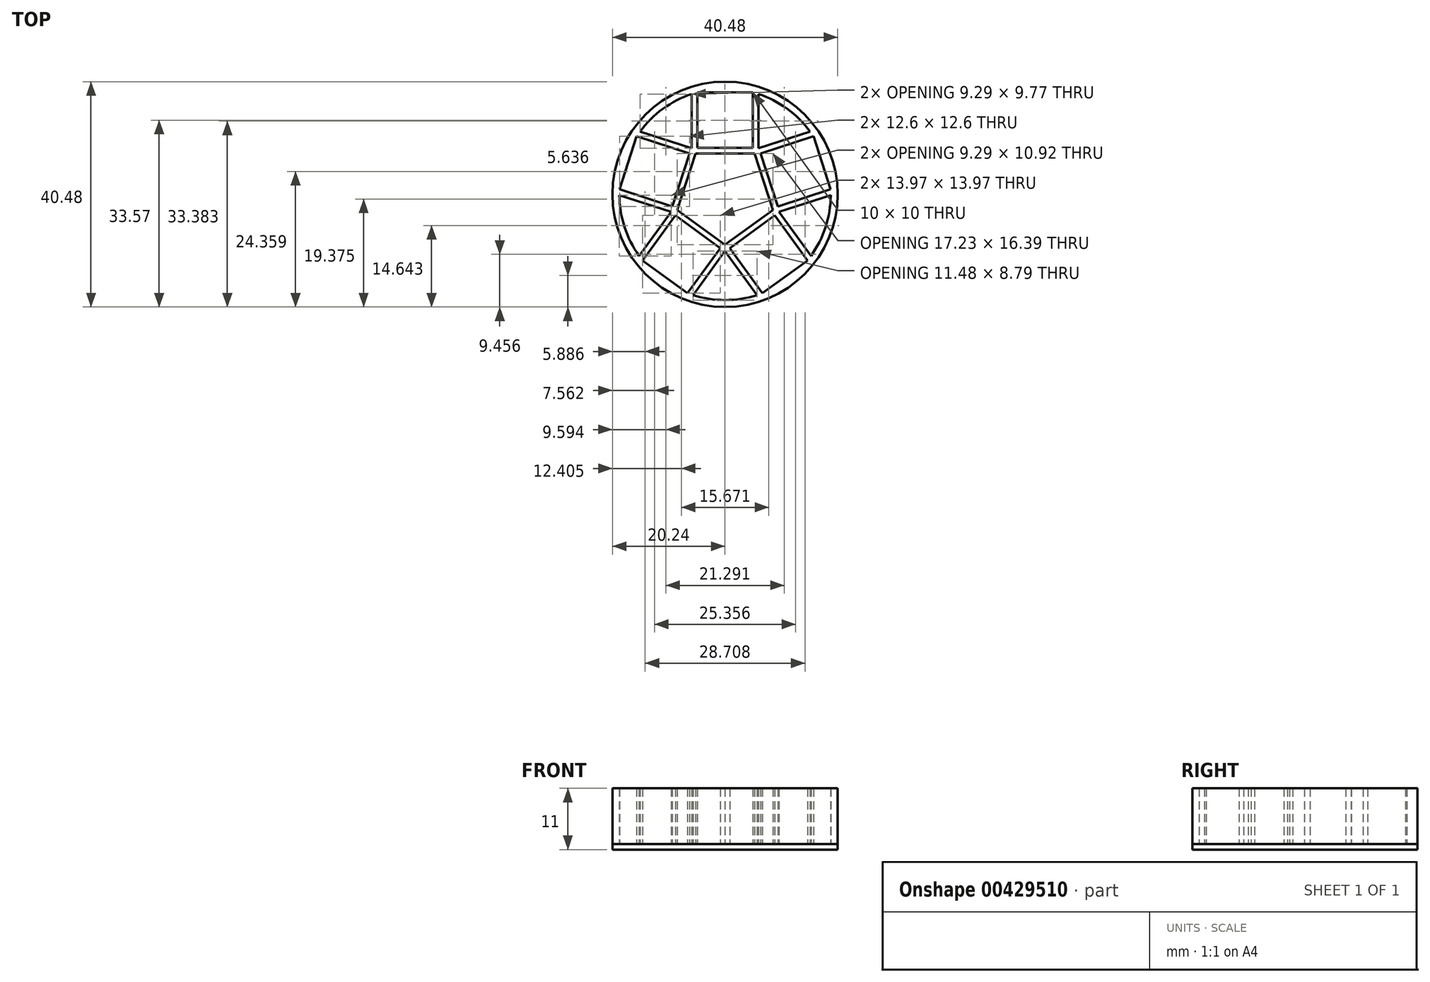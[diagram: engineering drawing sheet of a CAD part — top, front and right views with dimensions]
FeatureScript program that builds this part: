
annotation { "Feature Type Name" : "Feature", "Feature Type Description" : "" }
export const myFeature = defineFeature(function(context is Context, id is Id, definition is map)
    precondition{}
    {
        {
            var Q0;
            Q0=qCreatedBy(makeId("Top.planeOp"),FACE);
            var sketch = newSketch(context, id + "F0", { "sketchPlane" : qUnion([Q0])});
            skCircle(sketch, "E0", {"center": v(0, 0) * mm, "radius": 20.24 * mm});
            skCircle(sketch, "E1", {"center": v(0, 0) * mm, "radius": 19 * mm});
            skLineSegment(sketch, "E2.bottom", {"start": v(-6, 19.33) * mm, "end": v(6, 19.33) * mm});
            skLineSegment(sketch, "E2.top", {"start": v(-6, 7.33) * mm, "end": v(6, 7.33) * mm});
            skLineSegment(sketch, "E2.left", {"start": v(-6, 19.33) * mm, "end": v(-6, 7.33) * mm});
            skLineSegment(sketch, "E2.right", {"start": v(6, 19.33) * mm, "end": v(6, 7.33) * mm});
            skLineSegment(sketch, "E3.bottom", {"start": v(-5, 18.33) * mm, "end": v(5, 18.33) * mm});
            skLineSegment(sketch, "E3.top", {"start": v(-5, 8.33) * mm, "end": v(5, 8.33) * mm});
            skLineSegment(sketch, "E3.left", {"start": v(-5, 18.33) * mm, "end": v(-5, 8.33) * mm});
            skLineSegment(sketch, "E3.right", {"start": v(5, 18.33) * mm, "end": v(5, 8.33) * mm});
            skLineSegment(sketch, "E4.1.0", {"start": v(-20.24, 0.27) * mm, "end": v(-8.83, -3.44) * mm});
            skLineSegment(sketch, "E4.1.1", {"start": v(-18.98, 0.9) * mm, "end": v(-9.47, -2.18) * mm});
            skLineSegment(sketch, "E4.1.2", {"start": v(-9.47, -2.18) * mm, "end": v(-6.38, 7.33) * mm});
            skLineSegment(sketch, "E4.1.3", {"start": v(-8.83, -3.44) * mm, "end": v(-5.12, 7.97) * mm});
            skLineSegment(sketch, "E4.1.4", {"start": v(-16.53, 11.68) * mm, "end": v(-5.12, 7.97) * mm});
            skLineSegment(sketch, "E4.1.5", {"start": v(-15.89, 10.42) * mm, "end": v(-6.38, 7.33) * mm});
            skLineSegment(sketch, "E4.1.6", {"start": v(-18.98, 0.9) * mm, "end": v(-15.89, 10.42) * mm});
            skLineSegment(sketch, "E4.1.7", {"start": v(-20.24, 0.27) * mm, "end": v(-16.53, 11.68) * mm});
            skLineSegment(sketch, "E4.2.0", {"start": v(-6.5, -19.17) * mm, "end": v(0.55, -9.46) * mm});
            skLineSegment(sketch, "E4.2.1", {"start": v(-6.73, -17.77) * mm, "end": v(-0.85, -9.68) * mm});
            skLineSegment(sketch, "E4.2.2", {"start": v(-0.85, -9.68) * mm, "end": v(-8.94, -3.8) * mm});
            skLineSegment(sketch, "E4.2.3", {"start": v(0.55, -9.46) * mm, "end": v(-9.16, -2.4) * mm});
            skLineSegment(sketch, "E4.2.4", {"start": v(-16.22, -12.11) * mm, "end": v(-9.16, -2.4) * mm});
            skLineSegment(sketch, "E4.2.5", {"start": v(-14.82, -11.9) * mm, "end": v(-8.94, -3.8) * mm});
            skLineSegment(sketch, "E4.2.6", {"start": v(-6.73, -17.77) * mm, "end": v(-14.82, -11.9) * mm});
            skLineSegment(sketch, "E4.2.7", {"start": v(-6.5, -19.17) * mm, "end": v(-16.22, -12.11) * mm});
            skLineSegment(sketch, "E4.3.0", {"start": v(16.22, -12.11) * mm, "end": v(9.16, -2.4) * mm});
            skLineSegment(sketch, "E4.3.1", {"start": v(14.82, -11.9) * mm, "end": v(8.94, -3.8) * mm});
            skLineSegment(sketch, "E4.3.2", {"start": v(8.94, -3.8) * mm, "end": v(0.85, -9.68) * mm});
            skLineSegment(sketch, "E4.3.3", {"start": v(9.16, -2.4) * mm, "end": v(-0.55, -9.46) * mm});
            skLineSegment(sketch, "E4.3.4", {"start": v(6.5, -19.17) * mm, "end": v(-0.55, -9.46) * mm});
            skLineSegment(sketch, "E4.3.5", {"start": v(6.73, -17.77) * mm, "end": v(0.85, -9.68) * mm});
            skLineSegment(sketch, "E4.3.6", {"start": v(14.82, -11.9) * mm, "end": v(6.73, -17.77) * mm});
            skLineSegment(sketch, "E4.3.7", {"start": v(16.22, -12.11) * mm, "end": v(6.5, -19.17) * mm});
            skLineSegment(sketch, "E4.4.0", {"start": v(16.53, 11.68) * mm, "end": v(5.12, 7.97) * mm});
            skLineSegment(sketch, "E4.4.1", {"start": v(15.89, 10.42) * mm, "end": v(6.38, 7.33) * mm});
            skLineSegment(sketch, "E4.4.2", {"start": v(6.38, 7.33) * mm, "end": v(9.47, -2.18) * mm});
            skLineSegment(sketch, "E4.4.3", {"start": v(5.12, 7.97) * mm, "end": v(8.83, -3.44) * mm});
            skLineSegment(sketch, "E4.4.4", {"start": v(20.24, 0.27) * mm, "end": v(8.83, -3.44) * mm});
            skLineSegment(sketch, "E4.4.5", {"start": v(18.98, 0.9) * mm, "end": v(9.47, -2.18) * mm});
            skLineSegment(sketch, "E4.4.6", {"start": v(15.89, 10.42) * mm, "end": v(18.98, 0.9) * mm});
            skLineSegment(sketch, "E4.4.7", {"start": v(16.53, 11.68) * mm, "end": v(20.24, 0.27) * mm});
            skSolve(sketch);
        }
        {
            var Q0;
            Q0=makeQuery(id+"F0.imprint","IMPRINT",FACE,{"disambiguationData":[TD([[makeQuery(id+"F0.imprint","IMPRINT",EDGE,{"derivedFrom":sQuery(id+"F0.wireOp",EDGE,"E3.top")}),-1.0]])]});
            var Q1;
            {var subQ0=sQuery(id+"F0.wireOp",EDGE,"E4.2.0");var subQ5=sQuery(id+"F0.wireOp",EDGE,"E1");var subQ6=makeQuery(id+"F0.imprint","INTERSECT",VERTEX,{"derivedFrom":[subQ5,subQ0]});Q1=makeQuery(id+"F0.imprint","IMPRINT",FACE,{"disambiguationData":[TD([[makeQuery(id+"F0.imprint","IMPRINT",EDGE,{"disambiguationData":[TD([[subQ6,-1.0]])],"derivedFrom":subQ5}),-1.0]])]});}
            var Q2;
            {var subQ7=sQuery(id+"F0.wireOp",EDGE,"E4.2.1");Q2=makeQuery(id+"F0.imprint","IMPRINT",FACE,{"disambiguationData":[TD([[makeQuery(id+"F0.imprint","IMPRINT",EDGE,{"derivedFrom":subQ7}),-1.0]])]});}
            var Q3;
            Q3=makeQuery(id+"F0.imprint","IMPRINT",FACE,{"disambiguationData":[TD([[makeQuery(id+"F0.imprint","IMPRINT",EDGE,{"derivedFrom":sQuery(id+"F0.wireOp",EDGE,"E4.4.1")}),1.0]])]});
            var Q4;
            {var subQ5=sQuery(id+"F0.wireOp",EDGE,"E4.1.3");var subQ7=sQuery(id+"F0.wireOp",EDGE,"E2.top");var subQ8=makeQuery(id+"F0.imprint","INTERSECT",VERTEX,{"derivedFrom":[subQ7,subQ5]});Q4=makeQuery(id+"F0.imprint","IMPRINT",FACE,{"disambiguationData":[TD([[makeQuery(id+"F0.imprint","IMPRINT",EDGE,{"disambiguationData":[TD([[subQ8,-1.0]])],"derivedFrom":subQ7}),-1.0]])]});}
            var Q5;
            {var subQ0=sQuery(id+"F0.wireOp",EDGE,"E4.4.0");var subQ1=sQuery(id+"F0.wireOp",EDGE,"E1");var subQ2=makeQuery(id+"F0.imprint","INTERSECT",VERTEX,{"derivedFrom":[subQ1,subQ0]});Q5=makeQuery(id+"F0.imprint","IMPRINT",FACE,{"disambiguationData":[TD([[makeQuery(id+"F0.imprint","IMPRINT",EDGE,{"disambiguationData":[TD([[subQ2,-1.0]])],"derivedFrom":subQ1}),1.0]])]});}
            var Q6;
            Q6=makeQuery(id+"F0.imprint","IMPRINT",FACE,{"disambiguationData":[TD([[makeQuery(id+"F0.imprint","IMPRINT",EDGE,{"derivedFrom":sQuery(id+"F0.wireOp",EDGE,"E4.1.1")}),1.0]])]});
            var Q7;
            {var subQ0=sQuery(id+"F0.wireOp",EDGE,"E4.3.0");var subQ5=sQuery(id+"F0.wireOp",EDGE,"E1");var subQ7=makeQuery(id+"F0.imprint","INTERSECT",VERTEX,{"derivedFrom":[subQ5,subQ0]});Q7=makeQuery(id+"F0.imprint","IMPRINT",FACE,{"disambiguationData":[TD([[makeQuery(id+"F0.imprint","IMPRINT",EDGE,{"disambiguationData":[TD([[subQ7,-1.0]])],"derivedFrom":subQ5}),-1.0]])]});}
            var Q8;
            {var subQ12=sQuery(id+"F0.wireOp",EDGE,"E4.3.1");Q8=makeQuery(id+"F0.imprint","IMPRINT",FACE,{"disambiguationData":[TD([[makeQuery(id+"F0.imprint","IMPRINT",EDGE,{"derivedFrom":subQ12}),-1.0]])]});}
            var Q9;
            {var subQ0=sQuery(id+"F0.wireOp",EDGE,"E2.left");var subQ5=sQuery(id+"F0.wireOp",EDGE,"E1");var subQ6=makeQuery(id+"F0.imprint","INTERSECT",VERTEX,{"derivedFrom":[subQ5,subQ0]});Q9=makeQuery(id+"F0.imprint","IMPRINT",FACE,{"disambiguationData":[TD([[makeQuery(id+"F0.imprint","IMPRINT",EDGE,{"disambiguationData":[TD([[subQ6,-1.0]])],"derivedFrom":subQ5}),-1.0]])]});}
            var Q10;
            {var subQ0=sQuery(id+"F0.wireOp",EDGE,"E4.1.0");var subQ1=sQuery(id+"F0.wireOp",EDGE,"E1");var subQ2=makeQuery(id+"F0.imprint","INTERSECT",VERTEX,{"derivedFrom":[subQ1,subQ0]});Q10=makeQuery(id+"F0.imprint","IMPRINT",FACE,{"disambiguationData":[TD([[makeQuery(id+"F0.imprint","IMPRINT",EDGE,{"disambiguationData":[TD([[subQ2,-1.0]])],"derivedFrom":subQ1}),1.0]])]});}
            var Q11;
            Q11=makeQuery(id+"F0.imprint","IMPRINT",FACE,{"disambiguationData":[TD([[makeQuery(id+"F0.imprint","IMPRINT",EDGE,{"derivedFrom":sQuery(id+"F0.wireOp",EDGE,"E3.bottom")}),-1.0]])]});
            var Q12;
            {var subQ0=sQuery(id+"F0.wireOp",EDGE,"E4.3.7");Q12=makeQuery(id+"F0.imprint","IMPRINT",FACE,{"disambiguationData":[TD([[makeQuery(id+"F0.imprint","IMPRINT",EDGE,{"derivedFrom":subQ0}),1.0]])]});}
            var Q13;
            {var subQ0=sQuery(id+"F0.wireOp",EDGE,"E4.2.7");Q13=makeQuery(id+"F0.imprint","IMPRINT",FACE,{"disambiguationData":[TD([[makeQuery(id+"F0.imprint","IMPRINT",EDGE,{"derivedFrom":subQ0}),1.0]])]});}
            var Q14;
            {var subQ0=sQuery(id+"F0.wireOp",EDGE,"E4.1.7");Q14=makeQuery(id+"F0.imprint","IMPRINT",FACE,{"disambiguationData":[TD([[makeQuery(id+"F0.imprint","IMPRINT",EDGE,{"derivedFrom":subQ0}),1.0]])]});}
            var Q15;
            {var subQ0=sQuery(id+"F0.wireOp",EDGE,"E2.bottom");Q15=makeQuery(id+"F0.imprint","IMPRINT",FACE,{"disambiguationData":[TD([[makeQuery(id+"F0.imprint","IMPRINT",EDGE,{"derivedFrom":subQ0}),1.0]])]});}
            var Q16;
            {var subQ0=sQuery(id+"F0.wireOp",EDGE,"E4.4.7");Q16=makeQuery(id+"F0.imprint","IMPRINT",FACE,{"disambiguationData":[TD([[makeQuery(id+"F0.imprint","IMPRINT",EDGE,{"derivedFrom":subQ0}),1.0]])]});}
            var Q17;
            {var subQ0=sQuery(id+"F0.wireOp",EDGE,"E4.1.7");Q17=makeQuery(id+"F0.imprint","IMPRINT",FACE,{"disambiguationData":[TD([[makeQuery(id+"F0.imprint","IMPRINT",EDGE,{"derivedFrom":subQ0}),-1.0]])]});}
            var Q18;
            Q18=makeQuery(id+"F0.imprint","IMPRINT",FACE,{"disambiguationData":[TD([[makeQuery(id+"F0.imprint","IMPRINT",EDGE,{"derivedFrom":sQuery(id+"F0.wireOp",EDGE,"E4.2.1")}),1.0]])]});
            var Q19;
            {var subQ5=sQuery(id+"F0.wireOp",EDGE,"E4.4.1");Q19=makeQuery(id+"F0.imprint","IMPRINT",FACE,{"disambiguationData":[TD([[makeQuery(id+"F0.imprint","IMPRINT",EDGE,{"derivedFrom":subQ5}),-1.0]])]});}
            var Q20;
            {var subQ0=sQuery(id+"F0.wireOp",EDGE,"E4.3.0");var subQ1=sQuery(id+"F0.wireOp",EDGE,"E1");var subQ2=makeQuery(id+"F0.imprint","INTERSECT",VERTEX,{"derivedFrom":[subQ1,subQ0]});Q20=makeQuery(id+"F0.imprint","IMPRINT",FACE,{"disambiguationData":[TD([[makeQuery(id+"F0.imprint","IMPRINT",EDGE,{"disambiguationData":[TD([[subQ2,-1.0]])],"derivedFrom":subQ1}),1.0]])]});}
            var Q21;
            {var subQ0=sQuery(id+"F0.wireOp",EDGE,"E4.1.0");var subQ5=sQuery(id+"F0.wireOp",EDGE,"E1");var subQ6=makeQuery(id+"F0.imprint","INTERSECT",VERTEX,{"derivedFrom":[subQ5,subQ0]});Q21=makeQuery(id+"F0.imprint","IMPRINT",FACE,{"disambiguationData":[TD([[makeQuery(id+"F0.imprint","IMPRINT",EDGE,{"disambiguationData":[TD([[subQ6,-1.0]])],"derivedFrom":subQ5}),-1.0]])]});}
            var Q22;
            {var subQ15=sQuery(id+"F0.wireOp",EDGE,"E4.1.1");Q22=makeQuery(id+"F0.imprint","IMPRINT",FACE,{"disambiguationData":[TD([[makeQuery(id+"F0.imprint","IMPRINT",EDGE,{"derivedFrom":subQ15}),-1.0]])]});}
            var Q23;
            {var subQ3=sQuery(id+"F0.wireOp",EDGE,"E4.4.0");var subQ5=sQuery(id+"F0.wireOp",EDGE,"E1");var subQ6=makeQuery(id+"F0.imprint","INTERSECT",VERTEX,{"derivedFrom":[subQ5,subQ3]});Q23=makeQuery(id+"F0.imprint","IMPRINT",FACE,{"disambiguationData":[TD([[makeQuery(id+"F0.imprint","IMPRINT",EDGE,{"disambiguationData":[TD([[subQ6,-1.0]])],"derivedFrom":subQ5}),-1.0]])]});}
            var Q24;
            Q24=makeQuery(id+"F0.imprint","IMPRINT",FACE,{"disambiguationData":[TD([[makeQuery(id+"F0.imprint","IMPRINT",EDGE,{"derivedFrom":sQuery(id+"F0.wireOp",EDGE,"E4.3.1")}),1.0]])]});
            var Q25;
            {var subQ0=sQuery(id+"F0.wireOp",EDGE,"E4.2.0");var subQ1=sQuery(id+"F0.wireOp",EDGE,"E1");var subQ2=makeQuery(id+"F0.imprint","INTERSECT",VERTEX,{"derivedFrom":[subQ1,subQ0]});Q25=makeQuery(id+"F0.imprint","IMPRINT",FACE,{"disambiguationData":[TD([[makeQuery(id+"F0.imprint","IMPRINT",EDGE,{"disambiguationData":[TD([[subQ2,-1.0]])],"derivedFrom":subQ1}),1.0]])]});}
            var Q26;
            {var subQ0=sQuery(id+"F0.wireOp",EDGE,"E2.left");var subQ1=sQuery(id+"F0.wireOp",EDGE,"E1");var subQ2=makeQuery(id+"F0.imprint","INTERSECT",VERTEX,{"derivedFrom":[subQ1,subQ0]});Q26=makeQuery(id+"F0.imprint","IMPRINT",FACE,{"disambiguationData":[TD([[makeQuery(id+"F0.imprint","IMPRINT",EDGE,{"disambiguationData":[TD([[subQ2,-1.0]])],"derivedFrom":subQ1}),1.0]])]});}
            var Q27;
            {var subQ5=sQuery(id+"F0.wireOp",EDGE,"E4.4.7");Q27=makeQuery(id+"F0.imprint","IMPRINT",FACE,{"disambiguationData":[TD([[makeQuery(id+"F0.imprint","IMPRINT",EDGE,{"derivedFrom":subQ5}),-1.0]])]});}
            var Q28;
            {var subQ0=sQuery(id+"F0.wireOp",EDGE,"E2.bottom");Q28=makeQuery(id+"F0.imprint","IMPRINT",FACE,{"disambiguationData":[TD([[makeQuery(id+"F0.imprint","IMPRINT",EDGE,{"derivedFrom":subQ0}),-1.0]])]});}
            var Q29;
            {var subQ0=sQuery(id+"F0.wireOp",EDGE,"E4.3.7");Q29=makeQuery(id+"F0.imprint","IMPRINT",FACE,{"disambiguationData":[TD([[makeQuery(id+"F0.imprint","IMPRINT",EDGE,{"derivedFrom":subQ0}),-1.0]])]});}
            var Q30;
            {var subQ0=sQuery(id+"F0.wireOp",EDGE,"E4.2.7");Q30=makeQuery(id+"F0.imprint","IMPRINT",FACE,{"disambiguationData":[TD([[makeQuery(id+"F0.imprint","IMPRINT",EDGE,{"derivedFrom":subQ0}),-1.0]])]});}
            var Q31;
            {var subQ0=sQuery(id+"F0.wireOp",EDGE,"E4.3.6");Q31=makeQuery(id+"F0.imprint","IMPRINT",FACE,{"disambiguationData":[TD([[makeQuery(id+"F0.imprint","IMPRINT",EDGE,{"derivedFrom":subQ0}),1.0]])]});}
            var Q32;
            {var subQ0=sQuery(id+"F0.wireOp",EDGE,"E4.2.6");Q32=makeQuery(id+"F0.imprint","IMPRINT",FACE,{"disambiguationData":[TD([[makeQuery(id+"F0.imprint","IMPRINT",EDGE,{"derivedFrom":subQ0}),1.0]])]});}
            var Q33;
            {var subQ0=sQuery(id+"F0.wireOp",EDGE,"E4.1.6");Q33=makeQuery(id+"F0.imprint","IMPRINT",FACE,{"disambiguationData":[TD([[makeQuery(id+"F0.imprint","IMPRINT",EDGE,{"derivedFrom":subQ0}),1.0]])]});}
            var Q34;
            {var subQ0=sQuery(id+"F0.wireOp",EDGE,"E3.bottom");Q34=makeQuery(id+"F0.imprint","IMPRINT",FACE,{"disambiguationData":[TD([[makeQuery(id+"F0.imprint","IMPRINT",EDGE,{"derivedFrom":subQ0}),1.0]])]});}
            var Q35;
            {var subQ0=sQuery(id+"F0.wireOp",EDGE,"E4.4.6");Q35=makeQuery(id+"F0.imprint","IMPRINT",FACE,{"disambiguationData":[TD([[makeQuery(id+"F0.imprint","IMPRINT",EDGE,{"derivedFrom":subQ0}),1.0]])]});}
            var Q36;
            {var subQ0=sQuery(id+"F0.wireOp",EDGE,"E4.3.3");var subQ1=sQuery(id+"F0.wireOp",EDGE,"E4.3.0");var subQ2=makeQuery(id+"F0.imprint","INTERSECT",VERTEX,{"derivedFrom":[subQ1,subQ0]});Q36=makeQuery(id+"F0.imprint","IMPRINT",FACE,{"disambiguationData":[TD([[makeQuery(id+"F0.imprint","IMPRINT",EDGE,{"disambiguationData":[TD([[subQ2,1.0]])],"derivedFrom":subQ1}),1.0]])]});}
            var Q37;
            {var subQ0=sQuery(id+"F0.wireOp",EDGE,"E2.right");var subQ1=sQuery(id+"F0.wireOp",EDGE,"E2.top");var subQ2=makeQuery(id+"F0.imprint","INTERSECT",VERTEX,{"derivedFrom":[subQ1,subQ0]});Q37=makeQuery(id+"F0.imprint","IMPRINT",FACE,{"disambiguationData":[TD([[makeQuery(id+"F0.imprint","IMPRINT",EDGE,{"disambiguationData":[TD([[subQ2,1.0]])],"derivedFrom":subQ1}),1.0]])]});}
            var Q38;
            {var subQ0=sQuery(id+"F0.wireOp",EDGE,"E2.left");var subQ1=sQuery(id+"F0.wireOp",EDGE,"E2.top");var subQ2=makeQuery(id+"F0.imprint","INTERSECT",VERTEX,{"derivedFrom":[subQ1,subQ0]});Q38=makeQuery(id+"F0.imprint","IMPRINT",FACE,{"disambiguationData":[TD([[makeQuery(id+"F0.imprint","IMPRINT",EDGE,{"disambiguationData":[TD([[subQ2,-1.0]])],"derivedFrom":subQ1}),1.0]])]});}
            var Q39;
            {var subQ0=sQuery(id+"F0.wireOp",EDGE,"E4.1.3");var subQ1=sQuery(id+"F0.wireOp",EDGE,"E4.1.0");var subQ2=makeQuery(id+"F0.imprint","INTERSECT",VERTEX,{"derivedFrom":[subQ1,subQ0]});Q39=makeQuery(id+"F0.imprint","IMPRINT",FACE,{"disambiguationData":[TD([[makeQuery(id+"F0.imprint","IMPRINT",EDGE,{"disambiguationData":[TD([[subQ2,1.0]])],"derivedFrom":subQ1}),1.0]])]});}
            var Q40;
            {var subQ0=sQuery(id+"F0.wireOp",EDGE,"E4.2.3");var subQ1=sQuery(id+"F0.wireOp",EDGE,"E4.2.0");var subQ2=makeQuery(id+"F0.imprint","INTERSECT",VERTEX,{"derivedFrom":[subQ1,subQ0]});Q40=makeQuery(id+"F0.imprint","IMPRINT",FACE,{"disambiguationData":[TD([[makeQuery(id+"F0.imprint","IMPRINT",EDGE,{"disambiguationData":[TD([[subQ2,1.0]])],"derivedFrom":subQ1}),1.0]])]});}
            extrude(context, id + "F1", {"entities" : qUnion([Q0, Q1, Q2, Q3, Q4, Q5, Q6, Q7, Q8, Q9, Q10, Q11, Q12, Q13, Q14, Q15, Q16, Q17, Q18, Q19, Q20, Q21, Q22, Q23, Q24, Q25, Q26, Q27, Q28, Q29, Q30, Q31, Q32, Q33, Q34, Q35, Q36, Q37, Q38, Q39, Q40]), "depth" : -1 * mm, "offsetDistance" : 25 * mm});
        }
        {
            var Q0;
            {var subQ0=sQuery(id+"F0.wireOp",EDGE,"E2.left");var subQ5=sQuery(id+"F0.wireOp",EDGE,"E1");var subQ6=makeQuery(id+"F0.imprint","INTERSECT",VERTEX,{"derivedFrom":[subQ5,subQ0]});Q0=makeQuery(id+"F0.imprint","IMPRINT",FACE,{"disambiguationData":[TD([[makeQuery(id+"F0.imprint","IMPRINT",EDGE,{"disambiguationData":[TD([[subQ6,-1.0]])],"derivedFrom":subQ5}),-1.0]])]});}
            var Q1;
            Q1=makeQuery(id+"F0.imprint","IMPRINT",FACE,{"disambiguationData":[TD([[makeQuery(id+"F0.imprint","IMPRINT",EDGE,{"derivedFrom":sQuery(id+"F0.wireOp",EDGE,"E3.top")}),-1.0]])]});
            var Q2;
            {var subQ0=sQuery(id+"F0.wireOp",EDGE,"E4.1.6");Q2=makeQuery(id+"F0.imprint","IMPRINT",FACE,{"disambiguationData":[TD([[makeQuery(id+"F0.imprint","IMPRINT",EDGE,{"derivedFrom":subQ0}),1.0]])]});}
            var Q3;
            {var subQ0=sQuery(id+"F0.wireOp",EDGE,"E3.bottom");Q3=makeQuery(id+"F0.imprint","IMPRINT",FACE,{"disambiguationData":[TD([[makeQuery(id+"F0.imprint","IMPRINT",EDGE,{"derivedFrom":subQ0}),1.0]])]});}
            var Q4;
            {var subQ0=sQuery(id+"F0.wireOp",EDGE,"E4.4.6");Q4=makeQuery(id+"F0.imprint","IMPRINT",FACE,{"disambiguationData":[TD([[makeQuery(id+"F0.imprint","IMPRINT",EDGE,{"derivedFrom":subQ0}),1.0]])]});}
            var Q5;
            {var subQ0=sQuery(id+"F0.wireOp",EDGE,"E4.1.7");Q5=makeQuery(id+"F0.imprint","IMPRINT",FACE,{"disambiguationData":[TD([[makeQuery(id+"F0.imprint","IMPRINT",EDGE,{"derivedFrom":subQ0}),1.0]])]});}
            var Q6;
            {var subQ0=sQuery(id+"F0.wireOp",EDGE,"E2.bottom");Q6=makeQuery(id+"F0.imprint","IMPRINT",FACE,{"disambiguationData":[TD([[makeQuery(id+"F0.imprint","IMPRINT",EDGE,{"derivedFrom":subQ0}),1.0]])]});}
            var Q7;
            {var subQ0=sQuery(id+"F0.wireOp",EDGE,"E4.4.7");Q7=makeQuery(id+"F0.imprint","IMPRINT",FACE,{"disambiguationData":[TD([[makeQuery(id+"F0.imprint","IMPRINT",EDGE,{"derivedFrom":subQ0}),1.0]])]});}
            var Q8;
            {var subQ0=sQuery(id+"F0.wireOp",EDGE,"E4.1.7");Q8=makeQuery(id+"F0.imprint","IMPRINT",FACE,{"disambiguationData":[TD([[makeQuery(id+"F0.imprint","IMPRINT",EDGE,{"derivedFrom":subQ0}),-1.0]])]});}
            var Q9;
            {var subQ5=sQuery(id+"F0.wireOp",EDGE,"E4.4.1");Q9=makeQuery(id+"F0.imprint","IMPRINT",FACE,{"disambiguationData":[TD([[makeQuery(id+"F0.imprint","IMPRINT",EDGE,{"derivedFrom":subQ5}),-1.0]])]});}
            var Q10;
            {var subQ3=sQuery(id+"F0.wireOp",EDGE,"E4.4.0");var subQ5=sQuery(id+"F0.wireOp",EDGE,"E1");var subQ6=makeQuery(id+"F0.imprint","INTERSECT",VERTEX,{"derivedFrom":[subQ5,subQ3]});Q10=makeQuery(id+"F0.imprint","IMPRINT",FACE,{"disambiguationData":[TD([[makeQuery(id+"F0.imprint","IMPRINT",EDGE,{"disambiguationData":[TD([[subQ6,-1.0]])],"derivedFrom":subQ5}),-1.0]])]});}
            var Q11;
            {var subQ0=sQuery(id+"F0.wireOp",EDGE,"E4.1.0");var subQ5=sQuery(id+"F0.wireOp",EDGE,"E1");var subQ6=makeQuery(id+"F0.imprint","INTERSECT",VERTEX,{"derivedFrom":[subQ5,subQ0]});Q11=makeQuery(id+"F0.imprint","IMPRINT",FACE,{"disambiguationData":[TD([[makeQuery(id+"F0.imprint","IMPRINT",EDGE,{"disambiguationData":[TD([[subQ6,-1.0]])],"derivedFrom":subQ5}),-1.0]])]});}
            var Q12;
            {var subQ0=sQuery(id+"F0.wireOp",EDGE,"E4.3.0");var subQ5=sQuery(id+"F0.wireOp",EDGE,"E1");var subQ7=makeQuery(id+"F0.imprint","INTERSECT",VERTEX,{"derivedFrom":[subQ5,subQ0]});Q12=makeQuery(id+"F0.imprint","IMPRINT",FACE,{"disambiguationData":[TD([[makeQuery(id+"F0.imprint","IMPRINT",EDGE,{"disambiguationData":[TD([[subQ7,-1.0]])],"derivedFrom":subQ5}),-1.0]])]});}
            var Q13;
            {var subQ15=sQuery(id+"F0.wireOp",EDGE,"E4.1.1");Q13=makeQuery(id+"F0.imprint","IMPRINT",FACE,{"disambiguationData":[TD([[makeQuery(id+"F0.imprint","IMPRINT",EDGE,{"derivedFrom":subQ15}),-1.0]])]});}
            var Q14;
            {var subQ0=sQuery(id+"F0.wireOp",EDGE,"E2.bottom");Q14=makeQuery(id+"F0.imprint","IMPRINT",FACE,{"disambiguationData":[TD([[makeQuery(id+"F0.imprint","IMPRINT",EDGE,{"derivedFrom":subQ0}),-1.0]])]});}
            var Q15;
            {var subQ5=sQuery(id+"F0.wireOp",EDGE,"E4.4.7");Q15=makeQuery(id+"F0.imprint","IMPRINT",FACE,{"disambiguationData":[TD([[makeQuery(id+"F0.imprint","IMPRINT",EDGE,{"derivedFrom":subQ5}),-1.0]])]});}
            var Q16;
            {var subQ0=sQuery(id+"F0.wireOp",EDGE,"E4.3.3");var subQ1=sQuery(id+"F0.wireOp",EDGE,"E4.3.0");var subQ2=makeQuery(id+"F0.imprint","INTERSECT",VERTEX,{"derivedFrom":[subQ1,subQ0]});Q16=makeQuery(id+"F0.imprint","IMPRINT",FACE,{"disambiguationData":[TD([[makeQuery(id+"F0.imprint","IMPRINT",EDGE,{"disambiguationData":[TD([[subQ2,1.0]])],"derivedFrom":subQ1}),1.0]])]});}
            var Q17;
            {var subQ0=sQuery(id+"F0.wireOp",EDGE,"E2.right");var subQ1=sQuery(id+"F0.wireOp",EDGE,"E2.top");var subQ2=makeQuery(id+"F0.imprint","INTERSECT",VERTEX,{"derivedFrom":[subQ1,subQ0]});Q17=makeQuery(id+"F0.imprint","IMPRINT",FACE,{"disambiguationData":[TD([[makeQuery(id+"F0.imprint","IMPRINT",EDGE,{"disambiguationData":[TD([[subQ2,1.0]])],"derivedFrom":subQ1}),1.0]])]});}
            var Q18;
            {var subQ0=sQuery(id+"F0.wireOp",EDGE,"E2.left");var subQ1=sQuery(id+"F0.wireOp",EDGE,"E2.top");var subQ2=makeQuery(id+"F0.imprint","INTERSECT",VERTEX,{"derivedFrom":[subQ1,subQ0]});Q18=makeQuery(id+"F0.imprint","IMPRINT",FACE,{"disambiguationData":[TD([[makeQuery(id+"F0.imprint","IMPRINT",EDGE,{"disambiguationData":[TD([[subQ2,-1.0]])],"derivedFrom":subQ1}),1.0]])]});}
            var Q19;
            {var subQ0=sQuery(id+"F0.wireOp",EDGE,"E4.1.3");var subQ1=sQuery(id+"F0.wireOp",EDGE,"E4.1.0");var subQ2=makeQuery(id+"F0.imprint","INTERSECT",VERTEX,{"derivedFrom":[subQ1,subQ0]});Q19=makeQuery(id+"F0.imprint","IMPRINT",FACE,{"disambiguationData":[TD([[makeQuery(id+"F0.imprint","IMPRINT",EDGE,{"disambiguationData":[TD([[subQ2,1.0]])],"derivedFrom":subQ1}),1.0]])]});}
            var Q20;
            {var subQ0=sQuery(id+"F0.wireOp",EDGE,"E4.2.3");var subQ1=sQuery(id+"F0.wireOp",EDGE,"E4.2.0");var subQ2=makeQuery(id+"F0.imprint","INTERSECT",VERTEX,{"derivedFrom":[subQ1,subQ0]});Q20=makeQuery(id+"F0.imprint","IMPRINT",FACE,{"disambiguationData":[TD([[makeQuery(id+"F0.imprint","IMPRINT",EDGE,{"disambiguationData":[TD([[subQ2,1.0]])],"derivedFrom":subQ1}),1.0]])]});}
            var Q21;
            {var subQ0=sQuery(id+"F0.wireOp",EDGE,"E4.2.7");Q21=makeQuery(id+"F0.imprint","IMPRINT",FACE,{"disambiguationData":[TD([[makeQuery(id+"F0.imprint","IMPRINT",EDGE,{"derivedFrom":subQ0}),-1.0]])]});}
            var Q22;
            {var subQ7=sQuery(id+"F0.wireOp",EDGE,"E4.2.1");Q22=makeQuery(id+"F0.imprint","IMPRINT",FACE,{"disambiguationData":[TD([[makeQuery(id+"F0.imprint","IMPRINT",EDGE,{"derivedFrom":subQ7}),-1.0]])]});}
            var Q23;
            {var subQ0=sQuery(id+"F0.wireOp",EDGE,"E4.2.0");var subQ5=sQuery(id+"F0.wireOp",EDGE,"E1");var subQ6=makeQuery(id+"F0.imprint","INTERSECT",VERTEX,{"derivedFrom":[subQ5,subQ0]});Q23=makeQuery(id+"F0.imprint","IMPRINT",FACE,{"disambiguationData":[TD([[makeQuery(id+"F0.imprint","IMPRINT",EDGE,{"disambiguationData":[TD([[subQ6,-1.0]])],"derivedFrom":subQ5}),-1.0]])]});}
            var Q24;
            {var subQ0=sQuery(id+"F0.wireOp",EDGE,"E4.3.7");Q24=makeQuery(id+"F0.imprint","IMPRINT",FACE,{"disambiguationData":[TD([[makeQuery(id+"F0.imprint","IMPRINT",EDGE,{"derivedFrom":subQ0}),1.0]])]});}
            var Q25;
            {var subQ0=sQuery(id+"F0.wireOp",EDGE,"E4.2.7");Q25=makeQuery(id+"F0.imprint","IMPRINT",FACE,{"disambiguationData":[TD([[makeQuery(id+"F0.imprint","IMPRINT",EDGE,{"derivedFrom":subQ0}),1.0]])]});}
            var Q26;
            {var subQ12=sQuery(id+"F0.wireOp",EDGE,"E4.3.1");Q26=makeQuery(id+"F0.imprint","IMPRINT",FACE,{"disambiguationData":[TD([[makeQuery(id+"F0.imprint","IMPRINT",EDGE,{"derivedFrom":subQ12}),-1.0]])]});}
            var Q27;
            {var subQ0=sQuery(id+"F0.wireOp",EDGE,"E4.3.6");Q27=makeQuery(id+"F0.imprint","IMPRINT",FACE,{"disambiguationData":[TD([[makeQuery(id+"F0.imprint","IMPRINT",EDGE,{"derivedFrom":subQ0}),1.0]])]});}
            var Q28;
            {var subQ0=sQuery(id+"F0.wireOp",EDGE,"E4.2.6");Q28=makeQuery(id+"F0.imprint","IMPRINT",FACE,{"disambiguationData":[TD([[makeQuery(id+"F0.imprint","IMPRINT",EDGE,{"derivedFrom":subQ0}),1.0]])]});}
            var Q29;
            {var subQ0=sQuery(id+"F0.wireOp",EDGE,"E4.3.7");Q29=makeQuery(id+"F0.imprint","IMPRINT",FACE,{"disambiguationData":[TD([[makeQuery(id+"F0.imprint","IMPRINT",EDGE,{"derivedFrom":subQ0}),-1.0]])]});}
            extrude(context, id + "F2", {"entities" : qUnion([Q0, Q1, Q2, Q3, Q4, Q5, Q6, Q7, Q8, Q9, Q10, Q11, Q12, Q13, Q14, Q15, Q16, Q17, Q18, Q19, Q20, Q21, Q22, Q23, Q24, Q25, Q26, Q27, Q28, Q29]), "depth" : 10 * mm, "offsetDistance" : 25 * mm});
        }
    });
